# Revit family: Hitachi_RAC-YHA4_Outdoor_Unit_1116
name_source: partatom
category: Mechanical Equipment
revit_build: Autodesk Revit 2013 (Build: 20120221_2030(x64)
units: mm (PartAtom-declared; Revit-internal decimal feet)

## types (4) — shared parameters
Back Clearance = 100 mm  [stored 0.328084 ft]
Clearance = Default
Energy Star = Yes
Front Clearance = 700 mm  [stored 2.29659 ft]
Interconnecting Wires = 3 + E, 1.5 mm
Left Clearance = 100 mm  [stored 0.328084 ft]
Manufacturer = Temperzone / Hitachi
Material = Hitachi - Outdoor Unit
Outdoor Operating Temp. (cooling) C db = 46 to -10 C
Outdoor Operating Temp. (heating) C db = 21 to -15 C
Pipe Connection Size - Liquid = 6.35 mm
Pipe Length (min./max.) = 3m to 30m
Power Suppy = 240 / 1
Radius pipe Top LIQUID = 3 mm  [stored 0.00984252 ft]
Refrigerant Type = R410A
Right Clearance = 200 mm  [stored 0.656168 ft]
Top Clearance = 200 mm  [stored 0.656168 ft]
URL = www.temperzone.biz
Unit Depth = 298 mm  [stored 0.97769 ft]
Unit Width = 850 mm  [stored 2.78871 ft]

## per-type parameters (varying)
| type | Airflow - ExLow | Airflow - Hi | Airflow - Low | Airflow - Med | COP Heating | Cooling Capacity | Cooling Range | Description | EER Cooling | Heating Capacity | Heating Range | Height Refig Pipe (Top LIQUID) | Height Refrig Pipe (Bottom - GAS) | Model - Indoor | Pipe Connection Size - Gas | Pipe Height (max.) | Radius Pipe Bottom GAS | Recommended External Protection | Refrig Pipe Offset from Back | Refrigerant Pipe Charge Length | Sound Pressure Level (dbA) - Cool / Heat | Unit Height | Weight (kg) |
| RAC-50YHA4 | 70.0 L/s | 200.0 L/s | 100.0 L/s | 150.0 L/s | 4.04 | 5000 W | 1.2 - 5.8 kW | Hitachi Outdoor Unit RAC-50YHA4 | 3.44 | 6000 W | 1.2 - 6.8 kW | 170 mm | 96 mm  [stored 0.314961 ft] | RAS-50YHA4 | 12.7 mm | 10m | 6 mm  [stored 0.019685 ft] | 16 A | 201 mm  [stored 0.659449 ft] | 30m | 50 / 52 | 650 mm  [stored 2.13255 ft] | 45 |
| RAC-60YHA4 | 120.0 L/s | 270.0 L/s | 145.0 L/s | 200.0 L/s | 3.85 | 6000 W | 1.2 - 6.8 kW | Hitachi Outdoor Unit RAC-60YHA4 | 3.33 | 7000 W | 1.2 - 7.5 kW | 160 mm | 108 mm | RAS-60YHA4 | 12.7 mm | 20m | 6 mm  [stored 0.019685 ft] | 20 A | 191 mm  [stored 0.62664 ft] | 20m | 50 / 52 | 750 mm  [stored 2.46063 ft] | 52 |
| RAC-70YHA4 | 140.0 L/s | 260.0 L/s | 170.0 L/s | 210.0 L/s | 4.18 | 7000 W | 1.5 - 8.3 kW | Hitachi Outdoor Unit RAC-70YHA4 | 3.38 | 8000 W | 1.5 - 9.0 kW | 170 mm | 96 mm  [stored 0.314961 ft] | RAS-70YHA4 | 15.9 mm | 20m | 8 mm  [stored 0.0262467 ft] | 20 A | 201 mm  [stored 0.659449 ft] | 30m | 51 / 53 | 800 mm  [stored 2.62467 ft] | 52 |
| RAC-80YHA4 | 146.0 L/s | 250.0 L/s | 170.0 L/s | 210.0 L/s | 3.89 | 8000 W | 1.5 - 8.5 kW | Hitachi Outdoor Unit RAC-80YHA4 | 3.24 | 9000 W | 1.5 - 9.7 kW | 170 mm | 96 mm  [stored 0.314961 ft] | RAS-80YHA4 | 15.9 mm | 20m | 8 mm  [stored 0.0262467 ft] | 20 A | 201 mm  [stored 0.659449 ft] | 30m | 55 / 55 | 800 mm  [stored 2.62467 ft] | 52 |

note: column(s) folded — value = type name in every type: Model

note: [stored X ft] marks values corroborated as IEEE doubles in the binary element streams (Revit-internal decimal feet)

## geometry (parser evidence)
native form markers: Sweep x1
no freeform markers — native parametric forms only
